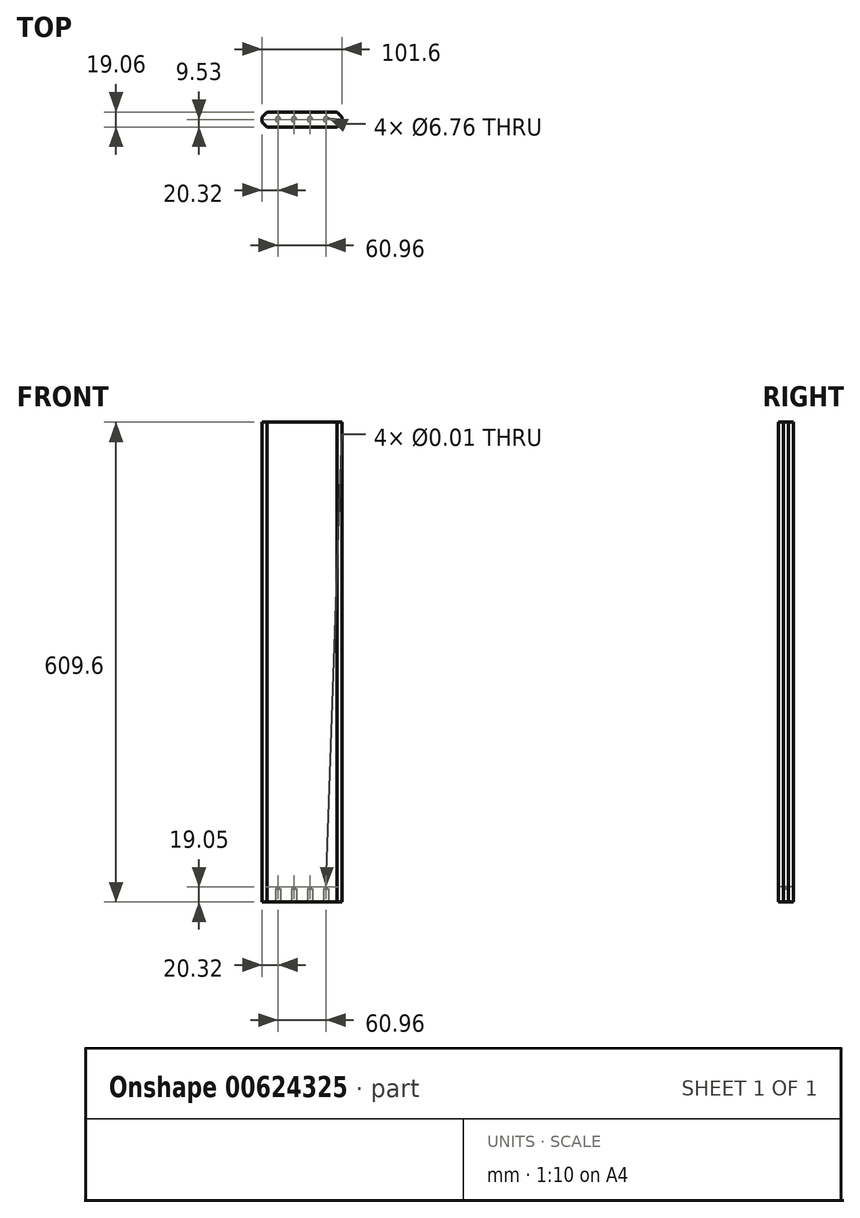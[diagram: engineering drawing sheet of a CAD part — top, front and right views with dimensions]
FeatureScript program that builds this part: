
annotation { "Feature Type Name" : "Feature", "Feature Type Description" : "" }
export const myFeature = defineFeature(function(context is Context, id is Id, definition is map)
    precondition{}
    {
        {
            var Q0;
            Q0=qCreatedBy(makeId("Front.planeOp"),FACE);
            var sketch = newSketch(context, id + "F0", { "sketchPlane" : qUnion([Q0])});
            skLineSegment(sketch, "E0.bottom", {"start": v(-50.8, 304.8) * mm, "end": v(50.8, 304.8) * mm});
            skLineSegment(sketch, "E0.top", {"start": v(-50.8, -304.8) * mm, "end": v(50.8, -304.8) * mm});
            skLineSegment(sketch, "E0.left", {"start": v(-50.8, 304.8) * mm, "end": v(-50.8, -304.8) * mm});
            skLineSegment(sketch, "E0.right", {"start": v(50.8, 304.8) * mm, "end": v(50.8, -304.8) * mm});
            skLineSegment(sketch, "E1", {"start": v(-50.8, 0) * mm, "end": v(50.8, 0) * mm, "construction": true});
            skLineSegment(sketch, "E2", {"start": v(0, 304.8) * mm, "end": v(0, -304.8) * mm, "construction": true});
            skSolve(sketch);
        }
        {
            var Q0;
            Q0=makeQuery(id+"F0.imprint","IMPRINT",FACE,{"disambiguationData":[TD([[makeQuery(id+"F0.imprint","IMPRINT",EDGE,{"derivedFrom":sQuery(id+"F0.wireOp",EDGE,"E0.bottom")}),-1.0]])]});
            extrude(context, id + "F1", {"entities" : qUnion([Q0]), "endBound" : BoundingType.SYMMETRIC, "depth" : 19.05 * mm, "offsetDistance" : 25.4 * mm});
        }
        {
            var Q0;
            Q0=makeQuery(id+"F1.opExtrude","CAP_FACE",FACE,{"disambiguationData":[OSD([sQuery(id+"F0.wireOp",EDGE,"E0.bottom"),sQuery(id+"F0.wireOp",EDGE,"E0.top"),sQuery(id+"F0.wireOp",EDGE,"E0.left"),sQuery(id+"F0.wireOp",EDGE,"E0.right")])],"isStart":false});
            var sketch = newSketch(context, id + "F2", { "sketchPlane" : qUnion([Q0])});
            skLineSegment(sketch, "E3", {"start": v(-50.8, -285.75) * mm, "end": v(50.8, -285.75) * mm, "construction": true});
            skPoint(sketch, "E4", {"position": v(-30.48, -285.75) * mm});
            skPoint(sketch, "E5.1.0.0", {"position": v(-10.16, -285.75) * mm});
            skPoint(sketch, "E5.2.0.0", {"position": v(10.16, -285.75) * mm});
            skPoint(sketch, "E5.3.0.0", {"position": v(30.48, -285.75) * mm});
            skLineSegment(sketch, "E5.direction1", {"start": v(-30.48, -285.75) * mm, "end": v(-10.16, -285.75) * mm, "construction": true});
            skSolve(sketch);
        }
        {
            var Q0;
            Q0=makeQuery(id+"F1.opExtrude","SWEPT_FACE",FACE,{"disambiguationData":[OSD([sQuery(id+"F0.wireOp",EDGE,"E0.top")])]});
            var sketch = newSketch(context, id + "F3", { "sketchPlane" : qUnion([Q0])});
            skLineSegment(sketch, "E6", {"start": v(-50.8, 0) * mm, "end": v(50.8, 0) * mm, "construction": true});
            skPoint(sketch, "E7", {"position": v(-30.48, 0) * mm});
            skPoint(sketch, "E8.1.0.0", {"position": v(-10.16, 0) * mm});
            skPoint(sketch, "E8.2.0.0", {"position": v(10.16, 0) * mm});
            skPoint(sketch, "E8.3.0.0", {"position": v(30.48, 0) * mm});
            skLineSegment(sketch, "E8.direction1", {"start": v(-30.48, 0) * mm, "end": v(-10.16, 0) * mm, "construction": true});
            skSolve(sketch);
        }
        {
            var Q0;
            Q0=sQuery(id+"F2.wireOp",VERTEX,"E4");
            var Q1;
            Q1=sQuery(id+"F2.wireOp",VERTEX,"E5.1.0.0");
            var Q2;
            Q2=sQuery(id+"F2.wireOp",VERTEX,"E5.2.0.0");
            var Q3;
            Q3=sQuery(id+"F2.wireOp",VERTEX,"E5.3.0.0");
            var Q4;
            Q4=makeQuery(id+"F1.opExtrude","SWEPT_BODY",BODY,{"disambiguationData":[OSD([sQuery(id+"F0.wireOp",EDGE,"E0.bottom"),sQuery(id+"F0.wireOp",EDGE,"E0.top"),sQuery(id+"F0.wireOp",EDGE,"E0.left"),sQuery(id+"F0.wireOp",EDGE,"E0.right")])]});
            hole(context, id + "F4", {"style" : HoleStyle.SIMPLE, "endStyle" : HoleEndStyle.BLIND, "standardTappedOrClearance" : lookupTablePath({ "standard" : "ANSI", "size" : "3/8 (0.38)", "type" : "Drilled" }), "standardBlindInLast" : lookupTablePath({ "standard" : "ANSI", "size" : "3/8", "type" : "Drilled" }), "holeDiameter" : 3 / 203.2 * mm, "majorDiameter" : 6.35 * mm, "holeDepth" : 16.54 * mm, "isTappedThrough" : true, "tappedDepth" : 12.7 * mm, "tapClearance" : 3, "startFromSketch" : true, "locations" : qUnion([Q0, Q1, Q2, Q3]), "scope" : qUnion([Q4])});
        }
        {
            var Q0;
            Q0=sQuery(id+"F3.wireOp",VERTEX,"E7");
            var Q1;
            Q1=sQuery(id+"F3.wireOp",VERTEX,"E8.1.0.0");
            var Q2;
            Q2=sQuery(id+"F3.wireOp",VERTEX,"E8.2.0.0");
            var Q3;
            Q3=sQuery(id+"F3.wireOp",VERTEX,"E8.3.0.0");
            var Q4;
            Q4=makeQuery(id+"F1.opExtrude","SWEPT_BODY",BODY,{"disambiguationData":[OSD([sQuery(id+"F0.wireOp",EDGE,"E0.bottom"),sQuery(id+"F0.wireOp",EDGE,"E0.top"),sQuery(id+"F0.wireOp",EDGE,"E0.left"),sQuery(id+"F0.wireOp",EDGE,"E0.right")])]});
            hole(context, id + "F5", {"style" : HoleStyle.SIMPLE, "endStyle" : HoleEndStyle.BLIND, "standardTappedOrClearance" : lookupTablePath({ "standard" : "ANSI", "fit" : "Normal (ASME)", "size" : "1/4", "type" : "Clearance" }), "standardBlindInLast" : lookupTablePath({ "fit" : "Free", "standard" : "ANSI", "size" : "1/4", "type" : "Clearance" }), "holeDiameter" : 6.76 * mm, "majorDiameter" : 6.35 * mm, "holeDepth" : 16.54 * mm, "isTappedThrough" : true, "tappedDepth" : 12.7 * mm, "tapClearance" : 3, "startFromSketch" : true, "locations" : qUnion([Q0, Q1, Q2, Q3]), "scope" : qUnion([Q4])});
        }
        {
            var Q0;
            Q0=makeQuery(id+"F1.opExtrude","CAP_EDGE",EDGE,{"disambiguationData":[OSD([sQuery(id+"F0.wireOp",EDGE,"E0.right")])],"isStart":false});
            var Q1;
            Q1=makeQuery(id+"F1.opExtrude","CAP_EDGE",EDGE,{"disambiguationData":[OSD([sQuery(id+"F0.wireOp",EDGE,"E0.right")])],"isStart":true});
            var Q2;
            Q2=makeQuery(id+"F1.opExtrude","CAP_EDGE",EDGE,{"disambiguationData":[OSD([sQuery(id+"F0.wireOp",EDGE,"E0.left")])],"isStart":false});
            var Q3;
            Q3=makeQuery(id+"F1.opExtrude","CAP_EDGE",EDGE,{"disambiguationData":[OSD([sQuery(id+"F0.wireOp",EDGE,"E0.left")])],"isStart":true});
            chamfer(context, id + "F6", {"entities" : qUnion([Q0, Q1, Q2, Q3]), "width" : 6.35 * mm, "tangentPropagation" : true});
        }
    });
